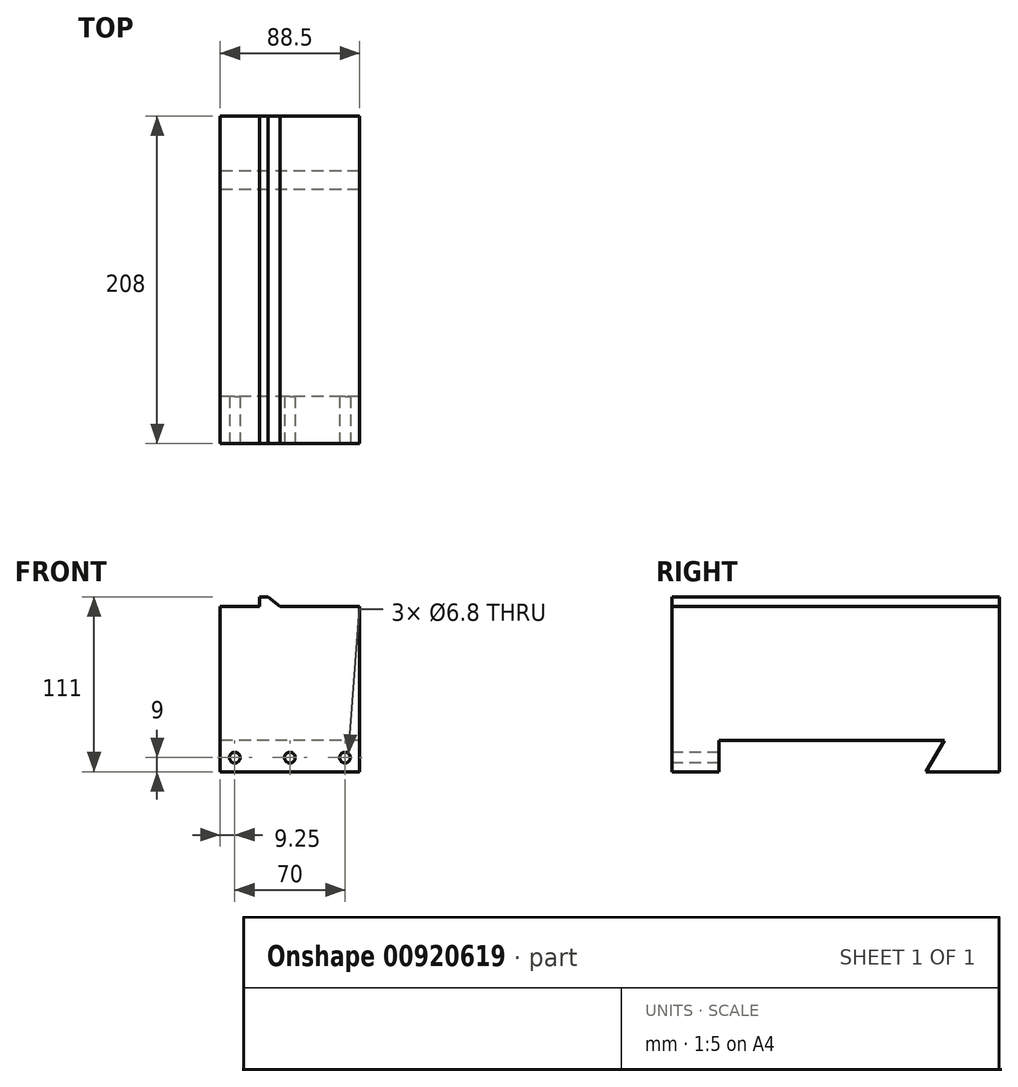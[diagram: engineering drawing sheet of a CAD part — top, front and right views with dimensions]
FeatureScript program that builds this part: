
annotation { "Feature Type Name" : "Feature", "Feature Type Description" : "" }
export const myFeature = defineFeature(function(context is Context, id is Id, definition is map)
    precondition{}
    {
        {
            var Q0;
            Q0=qCreatedBy(makeId("Right.planeOp"),FACE);
            var sketch = newSketch(context, id + "F0", { "sketchPlane" : qUnion([Q0])});
            skLineSegment(sketch, "E0", {"start": v(68.5, 0) * mm, "end": v(-74.5, 0) * mm});
            skLineSegment(sketch, "E1", {"start": v(-74.5, 0) * mm, "end": v(-74.5, -20) * mm});
            skLineSegment(sketch, "E2", {"start": v(-74.5, -20) * mm, "end": v(-104.5, -20) * mm});
            skLineSegment(sketch, "E3", {"start": v(-104.5, -20) * mm, "end": v(-104.5, 85) * mm});
            skLineSegment(sketch, "E4", {"start": v(-104.5, 85) * mm, "end": v(103.5, 85) * mm});
            skLineSegment(sketch, "E5", {"start": v(103.5, 85) * mm, "end": v(103.5, -20) * mm});
            skLineSegment(sketch, "E6", {"start": v(68.5, 0) * mm, "end": v(56.95, -20) * mm});
            skLineSegment(sketch, "E7", {"start": v(103.5, -20) * mm, "end": v(56.95, -20) * mm});
            skSolve(sketch);
        }
        {
            var Q0;
            Q0=makeQuery(id+"F0.imprint","IMPRINT",FACE,{"disambiguationData":[TD([[makeQuery(id+"F0.imprint","IMPRINT",EDGE,{"derivedFrom":sQuery(id+"F0.wireOp",EDGE,"E0")}),-1.0]])]});
            extrude(context, id + "F1", {"entities" : qUnion([Q0]), "depth" : 88.5 * mm, "offsetDistance" : 25 * mm});
        }
        {
            var Q0;
            Q0=makeQuery(id+"F1.opExtrude","SWEPT_FACE",FACE,{"disambiguationData":[OSD([sQuery(id+"F0.wireOp",EDGE,"E3")])]});
            var sketch = newSketch(context, id + "F2", { "sketchPlane" : qUnion([Q0])});
            skCircle(sketch, "E8", {"center": v(9.25, -11) * mm, "radius": 3.4 * mm});
            skCircle(sketch, "E9", {"center": v(44.25, -11) * mm, "radius": 3.4 * mm});
            skCircle(sketch, "E10", {"center": v(79.25, -11) * mm, "radius": 3.4 * mm});
            skSolve(sketch);
        }
        {
            var Q0;
            Q0=makeQuery(id+"F2.imprint","IMPRINT",FACE,{"disambiguationData":[TD([[makeQuery(id+"F2.imprint","IMPRINT",EDGE,{"derivedFrom":sQuery(id+"F2.wireOp",EDGE,"E8")}),1.0]])]});
            var Q1;
            Q1=makeQuery(id+"F2.imprint","IMPRINT",FACE,{"disambiguationData":[TD([[makeQuery(id+"F2.imprint","IMPRINT",EDGE,{"derivedFrom":sQuery(id+"F2.wireOp",EDGE,"E9")}),1.0]])]});
            var Q2;
            Q2=makeQuery(id+"F2.imprint","IMPRINT",FACE,{"disambiguationData":[TD([[makeQuery(id+"F2.imprint","IMPRINT",EDGE,{"derivedFrom":sQuery(id+"F2.wireOp",EDGE,"E10")}),1.0]])]});
            var Q3;
            Q3=makeQuery(id+"F1.opExtrude","SWEPT_FACE",FACE,{"disambiguationData":[OSD([sQuery(id+"F0.wireOp",EDGE,"E1")])]});
            extrude(context, id + "F3", {"entities" : qUnion([Q0, Q1, Q2]), "operationType" : NewBodyOperationType.REMOVE, "endBound" : BoundingType.UP_TO_SURFACE, "oppositeDirection" : true, "depth" : 25 * mm, "endBoundEntityFace" : qUnion([Q3]), "offsetDistance" : 25 * mm});
        }
        {
            var Q0;
            Q0=makeQuery(id+"F1.opExtrude","SWEPT_FACE",FACE,{"disambiguationData":[OSD([sQuery(id+"F0.wireOp",EDGE,"E3")])]});
            var sketch = newSketch(context, id + "F4", { "sketchPlane" : qUnion([Q0])});
            skLineSegment(sketch, "E11", {"start": v(25, 85) * mm, "end": v(25, 91) * mm});
            skLineSegment(sketch, "E12", {"start": v(25, 91) * mm, "end": v(30.5, 91) * mm});
            skLineSegment(sketch, "E13", {"start": v(30.5, 91) * mm, "end": v(38, 85) * mm});
            skLineSegment(sketch, "E14", {"start": v(38, 85) * mm, "end": v(25, 85) * mm});
            skSolve(sketch);
        }
        {
            var Q0;
            Q0=makeQuery(id+"F4.imprint","IMPRINT",FACE,{"disambiguationData":[TD([[makeQuery(id+"F4.imprint","IMPRINT",EDGE,{"derivedFrom":sQuery(id+"F4.wireOp",EDGE,"E11")}),-1.0]])]});
            var Q1;
            Q1=makeQuery(id+"F1.opExtrude","SWEPT_FACE",FACE,{"disambiguationData":[OSD([sQuery(id+"F0.wireOp",EDGE,"E5")])]});
            extrude(context, id + "F5", {"entities" : qUnion([Q0]), "operationType" : NewBodyOperationType.ADD, "endBound" : BoundingType.UP_TO_SURFACE, "oppositeDirection" : true, "depth" : 25 * mm, "endBoundEntityFace" : qUnion([Q1]), "offsetDistance" : 25 * mm});
        }
    });
